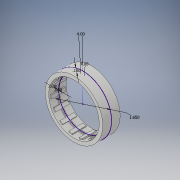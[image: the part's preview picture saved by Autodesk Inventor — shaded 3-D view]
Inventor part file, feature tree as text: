
AUTODESK INVENTOR PART (.ipt)
format: ipt  version: 2017 (Build 210142000, 142)  size: 230,912 bytes
history: native  units: in
note: dims shown in document units (in); Inventor stores cm internally (conversion verified against a paired STEP export)
features: extrude x3, sketch x1, pattern_circular x1
ambient origin geometry x8: Origin, YZ Plane, XZ Plane, XY Plane, X Axis, Y Axis, Z Axis, Center Point
bodies: Solid1 (feature_tree)
feature tree (5):
  sketch  "Sketch1"  dims[d0=1.65in d1=0.1in d2=0.5in d3=0.0in d4=0.0275in d5=0.0275in d7=0.03in d8=0.4in d9=0.0in d10=5.9055in d11=360.0deg d13=0.03in d14=0.05in d15=0.0in]
  extrude  "Extrusion1"  Depth=0.05in
  extrude  "Extrusion2"  Depth=0.5in TaperAngle=0.0deg
  pattern_circular  "Circular Pattern1"  [2 undecoded]
  extrude  "Extrusion3"  Depth=0.05in
note: 2 required parameter values undecoded (feature->parameter linkage not recoverable at this tier; creation-order binding heuristic only, values carry confidence <= 0.55)
